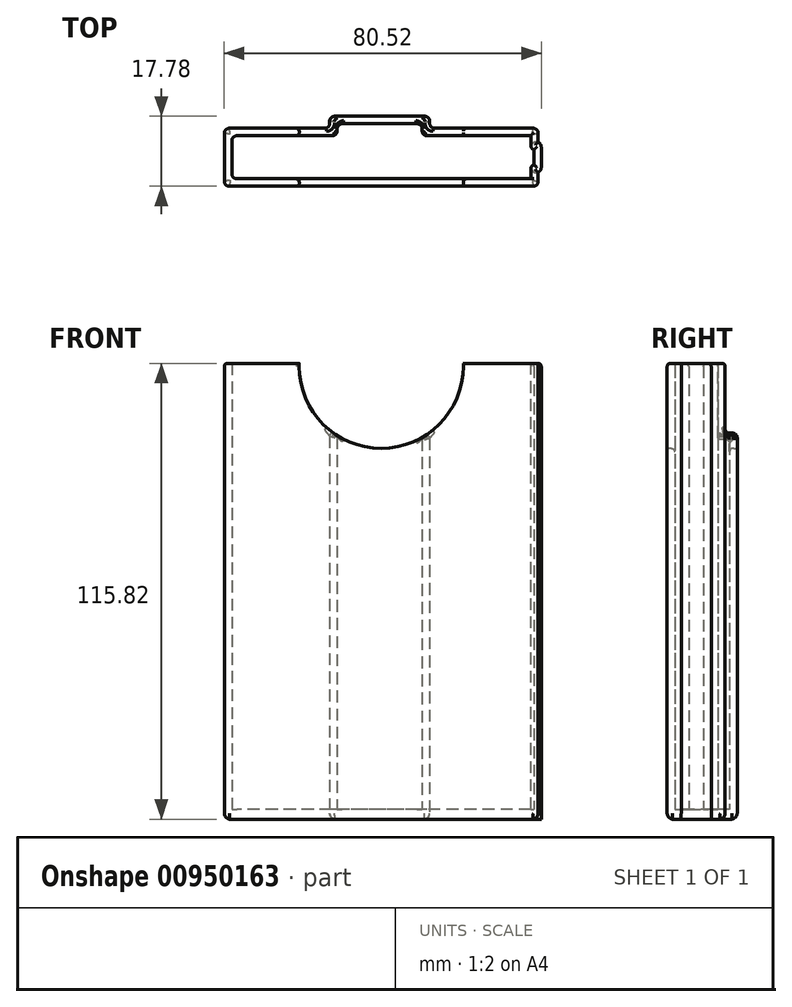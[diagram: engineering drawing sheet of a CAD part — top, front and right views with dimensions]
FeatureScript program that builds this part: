
annotation { "Feature Type Name" : "Feature", "Feature Type Description" : "" }
export const myFeature = defineFeature(function(context is Context, id is Id, definition is map)
    precondition{}
    {
        {
            var Q0;
            Q0=qCreatedBy(makeId("Top.planeOp"),FACE);
            var sketch = newSketch(context, id + "F0", { "sketchPlane" : qUnion([Q0])});
            skLineSegment(sketch, "E0.bottom", {"start": v(37.97, 5.46) * mm, "end": v(10.39, 5.46) * mm});
            skLineSegment(sketch, "E0.top", {"start": v(37.97, -5.46) * mm, "end": v(-37.97, -5.46) * mm});
            skLineSegment(sketch, "E0.right", {"start": v(-37.97, 5.46) * mm, "end": v(-37.97, -5.46) * mm});
            skPoint(sketch, "E0.middle", {"position": v(0, 0) * mm});
            skLineSegment(sketch, "E1", {"start": v(37.97, 5.46) * mm, "end": v(37.97, 1.9) * mm});
            skLineSegment(sketch, "E2", {"start": v(37.97, 1.9) * mm, "end": v(38.74, 1.9) * mm});
            skLineSegment(sketch, "E3", {"start": v(37.97, -5.46) * mm, "end": v(37.97, -1.9) * mm});
            skLineSegment(sketch, "E4", {"start": v(37.97, -1.9) * mm, "end": v(38.74, -1.9) * mm});
            skLineSegment(sketch, "E5", {"start": v(38.74, -1.9) * mm, "end": v(38.74, 1.9) * mm});
            skLineSegment(sketch, "E6", {"start": v(-0.4, 8.5) * mm, "end": v(10.39, 8.5) * mm});
            skLineSegment(sketch, "E7", {"start": v(10.39, 8.5) * mm, "end": v(10.39, 5.46) * mm});
            skLineSegment(sketch, "E8", {"start": v(-0.4, 8.5) * mm, "end": v(-11.2, 8.5) * mm});
            skLineSegment(sketch, "E9", {"start": v(-11.2, 8.5) * mm, "end": v(-11.2, 5.46) * mm});
            skLineSegment(sketch, "E10.trimOffspring", {"start": v(-11.2, 5.46) * mm, "end": v(-37.97, 5.46) * mm});
            skPoint(sketch, "E11.start.orphan", {"position": v(0, 5.46) * mm});
            skLineSegment(sketch, "E12.0", {"start": v(39.88, 7.37) * mm, "end": v(39.88, 3.81) * mm});
            skLineSegment(sketch, "E12.1", {"start": v(39.88, 3.81) * mm, "end": v(40.64, 3.81) * mm});
            skLineSegment(sketch, "E12.2", {"start": v(-13.1, 10.41) * mm, "end": v(-13.1, 7.37) * mm});
            skLineSegment(sketch, "E12.3", {"start": v(0, 10.41) * mm, "end": v(-13.1, 10.41) * mm});
            skLineSegment(sketch, "E12.4", {"start": v(0, 10.41) * mm, "end": v(12.3, 10.41) * mm});
            skLineSegment(sketch, "E12.5", {"start": v(12.3, 10.41) * mm, "end": v(12.3, 7.37) * mm});
            skLineSegment(sketch, "E12.6", {"start": v(-13.1, 7.37) * mm, "end": v(-39.88, 7.37) * mm});
            skLineSegment(sketch, "E12.7", {"start": v(-39.88, 7.37) * mm, "end": v(-39.88, -7.37) * mm});
            skLineSegment(sketch, "E12.8", {"start": v(39.88, 7.37) * mm, "end": v(12.3, 7.37) * mm});
            skLineSegment(sketch, "E12.9", {"start": v(39.88, -7.37) * mm, "end": v(-39.88, -7.37) * mm});
            skLineSegment(sketch, "E12.10", {"start": v(39.88, -7.37) * mm, "end": v(39.88, -3.81) * mm});
            skLineSegment(sketch, "E12.11", {"start": v(39.88, -3.81) * mm, "end": v(40.64, -3.81) * mm});
            skLineSegment(sketch, "E12.12", {"start": v(40.64, -3.81) * mm, "end": v(40.64, 3.81) * mm});
            skSolve(sketch);
        }
        {
            var Q0;
            Q0=makeQuery(id+"F0.imprint","IMPRINT",FACE,{"disambiguationData":[TD([[makeQuery(id+"F0.imprint","IMPRINT",EDGE,{"derivedFrom":sQuery(id+"F0.wireOp",EDGE,"E0.bottom")}),-1.0]])]});
            extrude(context, id + "F1", {"entities" : qUnion([Q0]), "depth" : 115.82 * mm, "offsetDistance" : 25.4 * mm});
        }
        {
            var Q0;
            Q0=makeQuery(id+"F1.opExtrude","CAP_FACE",FACE,{"disambiguationData":[OSD([sQuery(id+"F0.wireOp",EDGE,"E0.bottom"),sQuery(id+"F0.wireOp",EDGE,"E0.top"),sQuery(id+"F0.wireOp",EDGE,"E0.right"),sQuery(id+"F0.wireOp",EDGE,"E1"),sQuery(id+"F0.wireOp",EDGE,"E2"),sQuery(id+"F0.wireOp",EDGE,"E3"),sQuery(id+"F0.wireOp",EDGE,"E4"),sQuery(id+"F0.wireOp",EDGE,"E5"),sQuery(id+"F0.wireOp",EDGE,"E6"),sQuery(id+"F0.wireOp",EDGE,"E7"),sQuery(id+"F0.wireOp",EDGE,"E8"),sQuery(id+"F0.wireOp",EDGE,"E9"),sQuery(id+"F0.wireOp",EDGE,"E10.trimOffspring"),sQuery(id+"F0.wireOp",EDGE,"E12.0"),sQuery(id+"F0.wireOp",EDGE,"E12.1"),sQuery(id+"F0.wireOp",EDGE,"E12.2"),sQuery(id+"F0.wireOp",EDGE,"E12.3"),sQuery(id+"F0.wireOp",EDGE,"E12.4"),sQuery(id+"F0.wireOp",EDGE,"E12.5"),sQuery(id+"F0.wireOp",EDGE,"E12.6"),sQuery(id+"F0.wireOp",EDGE,"E12.7"),sQuery(id+"F0.wireOp",EDGE,"E12.8"),sQuery(id+"F0.wireOp",EDGE,"E12.9"),sQuery(id+"F0.wireOp",EDGE,"E12.10"),sQuery(id+"F0.wireOp",EDGE,"E12.11"),sQuery(id+"F0.wireOp",EDGE,"E12.12")])],"isStart":true});
            var sketch = newSketch(context, id + "F2", { "sketchPlane" : qUnion([Q0])});
            skLineSegment(sketch, "E13", {"start": v(-37.97, 5.46) * mm, "end": v(37.97, 5.46) * mm});
            skLineSegment(sketch, "E14", {"start": v(37.97, 5.46) * mm, "end": v(37.97, 1.9) * mm});
            skLineSegment(sketch, "E15", {"start": v(37.97, 1.9) * mm, "end": v(38.74, 1.9) * mm});
            skLineSegment(sketch, "E16", {"start": v(38.74, 1.9) * mm, "end": v(38.74, -1.9) * mm});
            skLineSegment(sketch, "E17", {"start": v(38.74, -1.9) * mm, "end": v(37.97, -1.9) * mm});
            skLineSegment(sketch, "E18", {"start": v(37.97, -1.9) * mm, "end": v(37.97, -5.46) * mm});
            skLineSegment(sketch, "E19", {"start": v(37.97, -5.46) * mm, "end": v(10.39, -5.46) * mm});
            skLineSegment(sketch, "E20", {"start": v(10.39, -5.46) * mm, "end": v(10.39, -8.5) * mm});
            skLineSegment(sketch, "E21", {"start": v(10.39, -8.5) * mm, "end": v(-11.2, -8.5) * mm});
            skLineSegment(sketch, "E22", {"start": v(-11.2, -8.5) * mm, "end": v(-11.2, -5.46) * mm});
            skLineSegment(sketch, "E23", {"start": v(-11.2, -5.46) * mm, "end": v(-37.97, -5.46) * mm});
            skLineSegment(sketch, "E24", {"start": v(-37.97, -5.46) * mm, "end": v(-37.97, 5.46) * mm});
            skSolve(sketch);
        }
        {
            var Q0;
            Q0=makeQuery(id+"F2.imprint","IMPRINT",FACE,{"disambiguationData":[TD([[makeQuery(id+"F2.imprint","IMPRINT",EDGE,{"derivedFrom":sQuery(id+"F2.wireOp",EDGE,"E13")}),1.0]])]});
            extrude(context, id + "F3", {"entities" : qUnion([Q0]), "operationType" : NewBodyOperationType.ADD, "oppositeDirection" : true, "depth" : 2.54 * mm, "offsetDistance" : 25.4 * mm});
        }
        {
            var Q0;
            Q0=makeQuery(id+"F1.opExtrude","SWEPT_EDGE",EDGE,{"disambiguationData":[OSD([sQuery(id+"F0.wireOp",EDGE,"E12.4"),sQuery(id+"F0.wireOp",EDGE,"E12.5")])]});
            var Q1;
            Q1=makeQuery(id+"F1.opExtrude","SWEPT_EDGE",EDGE,{"disambiguationData":[OSD([sQuery(id+"F0.wireOp",EDGE,"E12.5"),sQuery(id+"F0.wireOp",EDGE,"E12.8")])]});
            var Q2;
            Q2=makeQuery(id+"F1.opExtrude","SWEPT_EDGE",EDGE,{"disambiguationData":[OSD([sQuery(id+"F0.wireOp",EDGE,"E12.0"),sQuery(id+"F0.wireOp",EDGE,"E12.8")])]});
            var Q3;
            Q3=makeQuery(id+"F1.opExtrude","SWEPT_EDGE",EDGE,{"disambiguationData":[OSD([sQuery(id+"F0.wireOp",EDGE,"E12.9"),sQuery(id+"F0.wireOp",EDGE,"E12.10")])]});
            var Q4;
            Q4=makeQuery(id+"F1.opExtrude","SWEPT_EDGE",EDGE,{"disambiguationData":[OSD([sQuery(id+"F0.wireOp",EDGE,"E12.11"),sQuery(id+"F0.wireOp",EDGE,"E12.12")])]});
            var Q5;
            Q5=makeQuery(id+"F1.opExtrude","SWEPT_EDGE",EDGE,{"disambiguationData":[OSD([sQuery(id+"F0.wireOp",EDGE,"E12.1"),sQuery(id+"F0.wireOp",EDGE,"E12.12")])]});
            var Q6;
            Q6=makeQuery(id+"F1.opExtrude","SWEPT_EDGE",EDGE,{"disambiguationData":[OSD([sQuery(id+"F0.wireOp",EDGE,"E12.2"),sQuery(id+"F0.wireOp",EDGE,"E12.3")])]});
            var Q7;
            Q7=makeQuery(id+"F1.opExtrude","SWEPT_EDGE",EDGE,{"disambiguationData":[OSD([sQuery(id+"F0.wireOp",EDGE,"E12.2"),sQuery(id+"F0.wireOp",EDGE,"E12.6")])]});
            var Q8;
            Q8=makeQuery(id+"F1.opExtrude","SWEPT_EDGE",EDGE,{"disambiguationData":[OSD([sQuery(id+"F0.wireOp",EDGE,"E12.6"),sQuery(id+"F0.wireOp",EDGE,"E12.7")])]});
            var Q9;
            Q9=makeQuery(id+"F1.opExtrude","SWEPT_EDGE",EDGE,{"disambiguationData":[OSD([sQuery(id+"F0.wireOp",EDGE,"E12.7"),sQuery(id+"F0.wireOp",EDGE,"E12.9")])]});
            var Q10;
            Q10=makeQuery(id+"F1.opExtrude","SWEPT_EDGE",EDGE,{"disambiguationData":[OSD([sQuery(id+"F0.wireOp",EDGE,"E0.top"),sQuery(id+"F0.wireOp",EDGE,"E0.right")])]});
            var Q11;
            Q11=makeQuery(id+"F1.opExtrude","SWEPT_EDGE",EDGE,{"disambiguationData":[OSD([sQuery(id+"F0.wireOp",EDGE,"E0.right"),sQuery(id+"F0.wireOp",EDGE,"E10.trimOffspring")])]});
            var Q12;
            Q12=makeQuery(id+"F1.opExtrude","SWEPT_EDGE",EDGE,{"disambiguationData":[OSD([sQuery(id+"F0.wireOp",EDGE,"E9"),sQuery(id+"F0.wireOp",EDGE,"E10.trimOffspring")])]});
            var Q13;
            Q13=makeQuery(id+"F1.opExtrude","SWEPT_EDGE",EDGE,{"disambiguationData":[OSD([sQuery(id+"F0.wireOp",EDGE,"E8"),sQuery(id+"F0.wireOp",EDGE,"E9")])]});
            var Q14;
            Q14=makeQuery(id+"F1.opExtrude","SWEPT_EDGE",EDGE,{"disambiguationData":[OSD([sQuery(id+"F0.wireOp",EDGE,"E6"),sQuery(id+"F0.wireOp",EDGE,"E7")])]});
            var Q15;
            Q15=makeQuery(id+"F1.opExtrude","SWEPT_EDGE",EDGE,{"disambiguationData":[OSD([sQuery(id+"F0.wireOp",EDGE,"E0.bottom"),sQuery(id+"F0.wireOp",EDGE,"E7")])]});
            var Q16;
            Q16=makeQuery(id+"F1.opExtrude","SWEPT_EDGE",EDGE,{"disambiguationData":[OSD([sQuery(id+"F0.wireOp",EDGE,"E1"),sQuery(id+"F0.wireOp",EDGE,"E2")])]});
            var Q17;
            Q17=makeQuery(id+"F1.opExtrude","SWEPT_EDGE",EDGE,{"disambiguationData":[OSD([sQuery(id+"F0.wireOp",EDGE,"E3"),sQuery(id+"F0.wireOp",EDGE,"E4")])]});
            fillet(context, id + "F4", {"entities" : qUnion([Q0, Q1, Q2, Q3, Q4, Q5, Q6, Q7, Q8, Q9, Q10, Q11, Q12, Q13, Q14, Q15, Q16, Q17]), "radius" : 1.27 * mm, "tangentPropagation" : true, "allowEdgeOverflow" : false});
        }
        {
            var Q0;
            Q0=makeQuery(id+"F1.opExtrude","SWEPT_FACE",FACE,{"disambiguationData":[OSD([sQuery(id+"F0.wireOp",EDGE,"E12.9")])]});
            var sketch = newSketch(context, id + "F5", { "sketchPlane" : qUnion([Q0])});
            skPoint(sketch, "E25.0", {"position": v(-39.88, 115.82) * mm});
            skPoint(sketch, "E26.start.orphan", {"position": v(0, 115.82) * mm});
            skPoint(sketch, "E27.0", {"position": v(39.88, 115.82) * mm});
            skLineSegment(sketch, "E28", {"start": v(0, 115.82) * mm, "end": v(0, 115.08) * mm});
            skArc(sketch, "E29", {"start": v(-20.83, 115.82) * mm, "mid": v(0, 94.23) * mm, "end": v(20.83, 115.82) * mm});
            skLineSegment(sketch, "E30", {"start": v(-20.83, 115.82) * mm, "end": v(20.83, 115.82) * mm});
            skSolve(sketch);
        }
        {
            var Q0;
            {var subQ0=sQuery(id+"F5.wireOp",EDGE,"E29");Q0=makeQuery(id+"F5.imprint","IMPRINT",FACE,{"disambiguationData":[TD([[makeQuery(id+"F5.imprint","IMPRINT",EDGE,{"derivedFrom":subQ0}),1.0]])]});}
            extrude(context, id + "F6", {"entities" : qUnion([Q0]), "operationType" : NewBodyOperationType.REMOVE, "endBound" : BoundingType.THROUGH_ALL, "oppositeDirection" : true, "depth" : 25.4 * mm, "offsetDistance" : 25.4 * mm});
        }
        {
            var Q0;
            Q0=makeQuery(id+"F6.boolean.opBoolean","COPY",EDGE,{"derivedFrom":makeQuery(id+"F6.opExtrude","CAP_EDGE",EDGE,{"disambiguationData":[OSD([sQuery(id+"F5.wireOp",EDGE,"E29")])],"isStart":true})});
            var Q1;
            Q1=makeQuery(id+"F6.boolean.opBoolean","INTERSECT",EDGE,{"derivedFrom":[makeQuery(id+"F1.opExtrude","SWEPT_FACE",FACE,{"disambiguationData":[OSD([sQuery(id+"F0.wireOp",EDGE,"E0.top")])]}),makeQuery(id+"F6.opExtrude","SWEPT_FACE",FACE,{"disambiguationData":[OSD([sQuery(id+"F5.wireOp",EDGE,"E29")])]})]});
            fillet(context, id + "F7", {"entities" : qUnion([Q0, Q1]), "radius" : 0.89 * mm, "tangentPropagation" : true, "allowEdgeOverflow" : false});
        }
        {
            var Q0;
            Q0=makeQuery(id+"F1.opExtrude","CAP_EDGE",EDGE,{"disambiguationData":[OSD([sQuery(id+"F0.wireOp",EDGE,"E12.9")])],"isStart":true});
            fillet(context, id + "F8", {"entities" : qUnion([Q0]), "radius" : 1.52 * mm, "tangentPropagation" : true, "allowEdgeOverflow" : false});
        }
        {
            var Q0;
            Q0=makeQuery(id+"F6.boolean.opBoolean","INTERSECT",EDGE,{"derivedFrom":[makeQuery(id+"F1.opExtrude","SWEPT_FACE",FACE,{"disambiguationData":[OSD([sQuery(id+"F0.wireOp",EDGE,"E12.3"),sQuery(id+"F0.wireOp",EDGE,"E12.4")])]}),makeQuery(id+"F6.opExtrude","SWEPT_FACE",FACE,{"disambiguationData":[OSD([sQuery(id+"F5.wireOp",EDGE,"E29")])]})]});
            var Q1;
            Q1=makeQuery(id+"F1.opExtrude","CAP_EDGE",EDGE,{"disambiguationData":[OSD([sQuery(id+"F0.wireOp",EDGE,"E12.7")])],"isStart":false});
            var Q2;
            Q2=makeQuery(id+"F1.opExtrude","CAP_EDGE",EDGE,{"disambiguationData":[OSD([sQuery(id+"F0.wireOp",EDGE,"E12.8")])],"isStart":false});
            var Q3;
            {var subQ0=sQuery(id+"F0.wireOp",EDGE,"E12.10");var subQ1=sQuery(id+"F0.wireOp",EDGE,"E12.9");Q3=makeQuery(id+"F6.boolean.opBoolean","SPLIT",EDGE,{"disambiguationData":[TD([makeQuery(id+"F4.opFillet","BLEND_FACE",FACE,{"disambiguationData":[OSD([subQ1,subQ0])]})])],"derivedFrom":makeQuery(id+"F1.opExtrude","CAP_EDGE",EDGE,{"disambiguationData":[OSD([subQ1])],"isStart":false})});}
            var Q4;
            Q4=makeQuery(id+"F1.opExtrude","CAP_EDGE",EDGE,{"disambiguationData":[OSD([sQuery(id+"F0.wireOp",EDGE,"E12.12")])],"isStart":false});
            var Q5;
            Q5=makeQuery(id+"F6.boolean.opBoolean","INTERSECT",EDGE,{"derivedFrom":[makeQuery(id+"F1.opExtrude","SWEPT_FACE",FACE,{"disambiguationData":[OSD([sQuery(id+"F0.wireOp",EDGE,"E10.trimOffspring")])]}),makeQuery(id+"F6.opExtrude","SWEPT_FACE",FACE,{"disambiguationData":[OSD([sQuery(id+"F5.wireOp",EDGE,"E29")])]})]});
            var Q6;
            Q6=makeQuery(id+"F1.opExtrude","CAP_EDGE",EDGE,{"disambiguationData":[OSD([sQuery(id+"F0.wireOp",EDGE,"E0.bottom")])],"isStart":false});
            var Q7;
            Q7=makeQuery(id+"F1.opExtrude","CAP_EDGE",EDGE,{"disambiguationData":[OSD([sQuery(id+"F0.wireOp",EDGE,"E5")])],"isStart":false});
            var Q8;
            Q8=makeQuery(id+"F1.opExtrude","CAP_EDGE",EDGE,{"disambiguationData":[OSD([sQuery(id+"F0.wireOp",EDGE,"E1")])],"isStart":false});
            var Q9;
            Q9=makeQuery(id+"F1.opExtrude","CAP_EDGE",EDGE,{"disambiguationData":[OSD([sQuery(id+"F0.wireOp",EDGE,"E3")])],"isStart":false});
            var Q10;
            {var subQ0=sQuery(id+"F0.wireOp",EDGE,"E12.9");var subQ2=sQuery(id+"F0.wireOp",EDGE,"E10.trimOffspring");var subQ3=sQuery(id+"F5.wireOp",EDGE,"E29");var subQ4=sQuery(id+"F5.wireOp",EDGE,"E30");Q10=makeQuery(id+"F6.boolean.opBoolean","COPY",EDGE,{"disambiguationData":[TD([makeQuery(id+"F1.opExtrude","SWEPT_FACE",FACE,{"disambiguationData":[OSD([subQ2])]})])],"derivedFrom":makeQuery(id+"F6.opExtrude","SWEPT_EDGE",EDGE,{"disambiguationData":[OSD([subQ0,subQ3,subQ4]),TDD([makeQuery(id+"F5.imprint","INTERSECT",VERTEX,{"disambiguationData":[OD(0.0)],"derivedFrom":[makeQuery(id+"F1.opExtrude","CAP_EDGE",EDGE,{"disambiguationData":[OSD([subQ0])],"isStart":false}),subQ3,subQ4]})])]})});}
            var Q11;
            {var subQ0=sQuery(id+"F0.wireOp",EDGE,"E0.bottom");var subQ1=sQuery(id+"F0.wireOp",EDGE,"E12.9");var subQ3=sQuery(id+"F5.wireOp",EDGE,"E29");var subQ4=sQuery(id+"F5.wireOp",EDGE,"E30");Q11=makeQuery(id+"F6.boolean.opBoolean","COPY",EDGE,{"disambiguationData":[TD([makeQuery(id+"F1.opExtrude","SWEPT_FACE",FACE,{"disambiguationData":[OSD([subQ0])]})])],"derivedFrom":makeQuery(id+"F6.opExtrude","SWEPT_EDGE",EDGE,{"disambiguationData":[OSD([subQ1,subQ3,subQ4]),TDD([makeQuery(id+"F5.imprint","INTERSECT",VERTEX,{"disambiguationData":[OD(1.0)],"derivedFrom":[makeQuery(id+"F1.opExtrude","CAP_EDGE",EDGE,{"disambiguationData":[OSD([subQ1])],"isStart":false}),subQ3,subQ4]})])]})});}
            fillet(context, id + "F9", {"entities" : qUnion([Q0, Q1, Q2, Q3, Q4, Q5, Q6, Q7, Q8, Q9, Q10, Q11]), "radius" : 0.76 * mm, "tangentPropagation" : true, "allowEdgeOverflow" : false});
        }
    });
